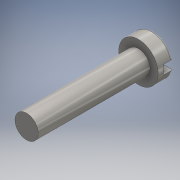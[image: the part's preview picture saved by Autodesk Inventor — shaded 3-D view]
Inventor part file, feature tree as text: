
AUTODESK INVENTOR PART (.ipt)
format: ipt  version: 2016 (Build 200138000, 138)  size: 140,800 bytes
history: native  units: mm
features: extrude x3, sketch x3, fillet x1
ambient origin geometry x8: Origin, YZ Plane, XZ Plane, XY Plane, X Axis, Y Axis, Z Axis, Center Point
bodies: Solid1 (feature_tree)
feature tree (7):
  extrude  "Extrusion1"  Depth=24.0mm TaperAngle=0.0deg
  extrude  "Extrusion2"  Depth=3.2mm TaperAngle=0.0deg
  extrude  "Extrusion3"  Depth=0.4mm
  fillet  "Fillet1"  Radius=5.0mm
  sketch  "Sketch1"  dims[d0=5.0mm d1=24.0mm d2=0.0mm]
  sketch  "Sketch2"  dims[d3=8.45mm d4=3.2mm d5=0.0mm]
  sketch  "Sketch3"  dims[d6=10.0mm d7=2.0mm d8=5.0mm d9=1.0mm d10=2.0mm d11=0.0mm d12=0.4mm]
